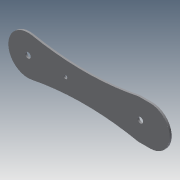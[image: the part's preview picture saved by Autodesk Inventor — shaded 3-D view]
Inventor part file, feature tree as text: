
AUTODESK INVENTOR PART (.ipt)
format: ipt  version: 2013 (Build 170138000, 138)  size: 142,336 bytes
history: native  units: mm
features: sketch x7, extrude x6
ambient origin geometry x8: Origin, YZ Plane, XZ Plane, XY Plane, X Axis, Y Axis, Z Axis, Center Point
bodies: Solid1 (feature_tree)
feature tree (13):
  extrude  "Extrusion1"  Depth=42.0mm
  sketch  "Sketch2"  dims[d8=2.0mm d9=0.0mm d27=10.5mm]
  extrude  "Extrusion2"  Depth=10.5mm
  extrude  "Extrusion3"  Depth=6.0mm
  extrude  "Extrusion4"  Depth=6.0mm
  extrude  "Extrusion5"  Depth=4.0mm
  extrude  "Extrusion6"  Depth=2.0mm TaperAngle=0.0deg
  sketch  "Sketch1"  dims[d3=42.0mm d5=42.0mm]
  sketch  "Sketch3"  dims[d28=2.0mm d29=0.0mm d30=6.0mm]
  sketch  "Sketch4"  dims[d31=10.5mm d32=6.0mm]
  sketch  "Sketch5"  dims[d33=40.0mm d34=4.0mm]
  sketch  "Sketch6"  dims[d35=2.0mm d36=0.0mm d37=2.0mm d38=0.0mm]
  sketch  "Sketch7"  dims[d39=40.0mm d40=6.0mm d41=2.0mm d42=0.0mm d43=6.0mm d44=2.0mm d45=0.0mm]
